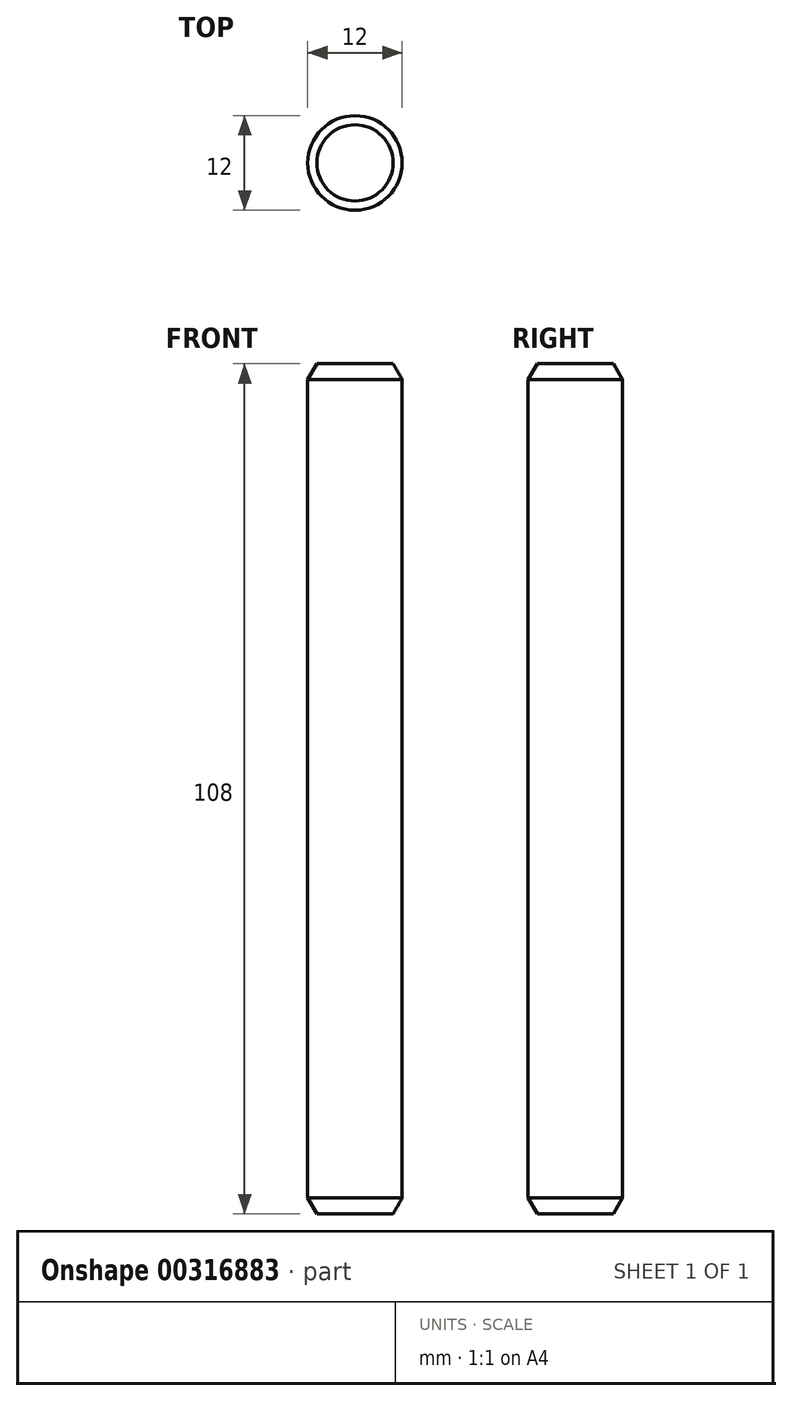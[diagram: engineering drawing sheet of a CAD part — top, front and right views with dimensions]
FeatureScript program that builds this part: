
annotation { "Feature Type Name" : "Feature", "Feature Type Description" : "" }
export const myFeature = defineFeature(function(context is Context, id is Id, definition is map)
    precondition{}
    {
        {
            var Q0;
            Q0=qCreatedBy(makeId("Top.planeOp"),FACE);
            var sketch = newSketch(context, id + "F0", { "sketchPlane" : qUnion([Q0])});
            skCircle(sketch, "E0", {"center": v(0, 0) * mm, "radius": 6 * mm});
            skSolve(sketch);
        }
        {
            var Q0;
            Q0 = qSketchRegion(id + "F0", true);
            extrude(context, id + "F1", {"entities" : qUnion([Q0]), "depth" : 108 * mm});
        }
        {
            var Q0;
            Q0=makeQuery(id+"F1.opExtrude","SWEPT_FACE",FACE,{"disambiguationData":[OSD([sQuery(id+"F0.wireOp",EDGE,"E0")])]});
            chamfer(context, id + "F2", {"entities" : qUnion([Q0]), "chamferType" : ChamferType.OFFSET_ANGLE, "width" : 2 * mm, "oppositeDirection" : false, "angle" : 30 * degree, "tangentPropagation" : true});
        }
    });
